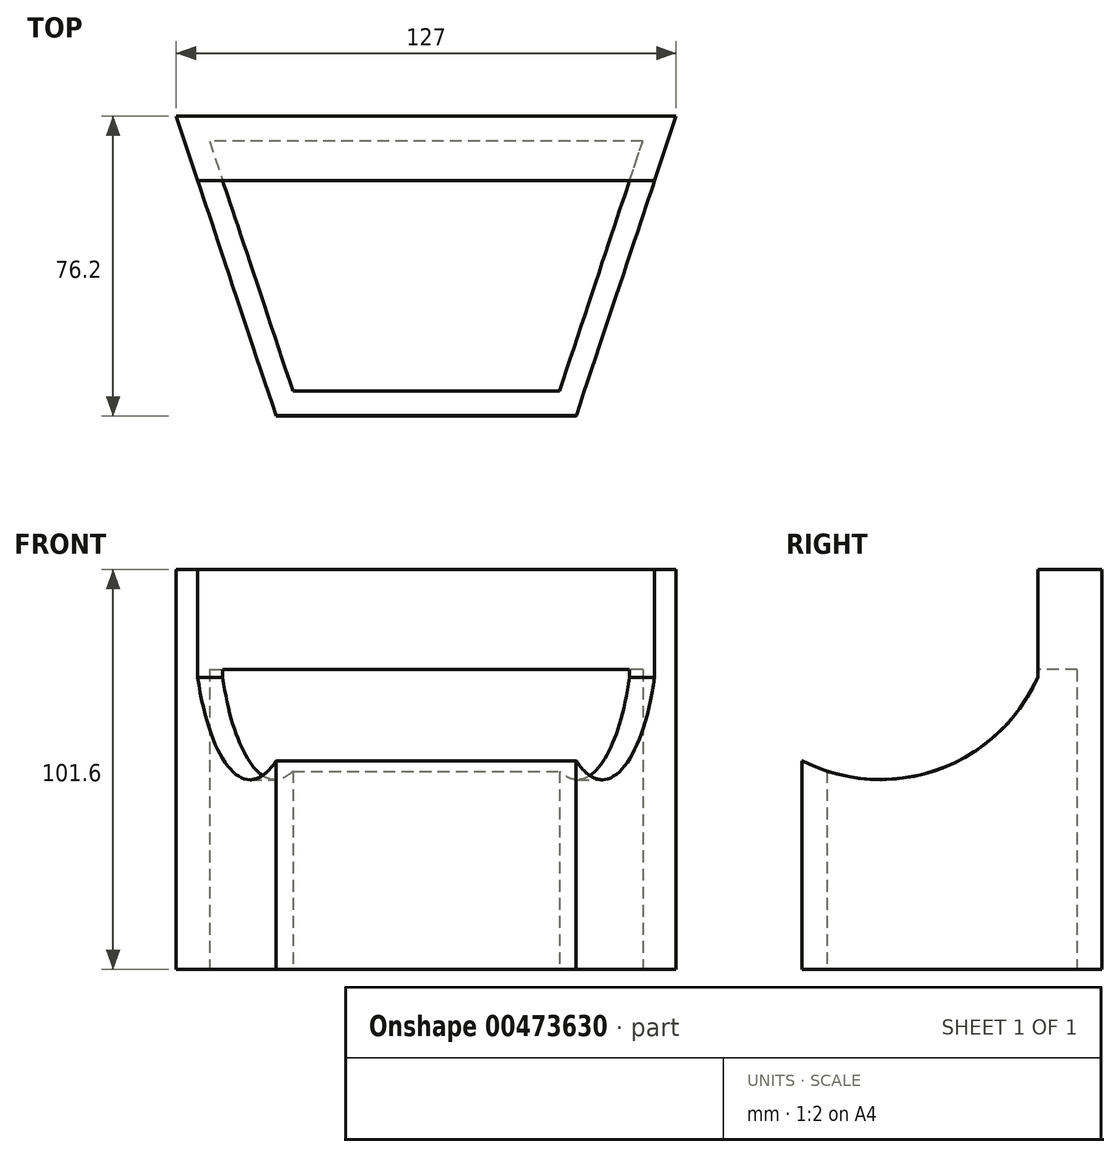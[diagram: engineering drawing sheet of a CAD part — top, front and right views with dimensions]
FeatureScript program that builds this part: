
annotation { "Feature Type Name" : "Feature", "Feature Type Description" : "" }
export const myFeature = defineFeature(function(context is Context, id is Id, definition is map)
    precondition{}
    {
        {
            var Q0;
            Q0=qCreatedBy(makeId("Top.planeOp"),FACE);
            var sketch = newSketch(context, id + "F0", { "sketchPlane" : qUnion([Q0])});
            skLineSegment(sketch, "E0.bottom", {"start": v(-38.1, -62.14) * mm, "end": v(38.1, -62.14) * mm});
            skLineSegment(sketch, "E1", {"start": v(-63.5, 14.06) * mm, "end": v(63.5, 14.06) * mm});
            skLineSegment(sketch, "E2", {"start": v(63.5, 14.06) * mm, "end": v(38.1, -62.14) * mm});
            skLineSegment(sketch, "E3", {"start": v(-38.1, -62.14) * mm, "end": v(-63.5, 14.06) * mm});
            skPoint(sketch, "E4", {"position": v(0, 14.06) * mm});
            skSolve(sketch);
        }
        {
            var Q0;
            Q0=makeQuery(id+"F0.imprint","IMPRINT",FACE,{"disambiguationData":[TD([[makeQuery(id+"F0.imprint","IMPRINT",EDGE,{"derivedFrom":sQuery(id+"F0.wireOp",EDGE,"E0.bottom")}),1.0]])]});
            extrude(context, id + "F1", {"entities" : qUnion([Q0]), "depth" : 101.6 * mm});
        }
        {
            var Q0;
            Q0=qCreatedBy(makeId("Right.planeOp"),FACE);
            cPlane(context, id + "F2", {"entities" : qUnion([Q0]), "cplaneType" : CPlaneType.OFFSET, "offset" : 63.5 * mm, "width" : 152.4 * mm, "height" : 152.4 * mm});
        }
        {
            var Q0;
            Q0=qCreatedBy(id+"F2.planeOp",FACE);
            var sketch = newSketch(context, id + "F3", { "sketchPlane" : qUnion([Q0])});
            skArc(sketch, "E5", {"start": v(-33.98, 110.4) * mm, "mid": v(-46.42, 109.44) * mm, "end": v(-57.74, 104.2) * mm});
            skLineSegment(sketch, "E6", {"start": v(-2.29, 74.18) * mm, "end": v(-2.29, 110.4) * mm});
            skLineSegment(sketch, "E7", {"start": v(-2.29, 110.4) * mm, "end": v(-33.98, 110.4) * mm});
            skPoint(sketch, "E8.top.end.orphan", {"position": v(13.85, 0) * mm});
            skLineSegment(sketch, "E9.bottom", {"start": v(-68.36, 104.2) * mm, "end": v(-57.74, 104.2) * mm});
            skLineSegment(sketch, "E9.left", {"start": v(-68.36, 104.2) * mm, "end": v(-68.36, 91.7) * mm});
            skLineSegment(sketch, "E10", {"start": v(-68.36, 91.7) * mm, "end": v(-68.36, 52.96) * mm});
            skLineSegment(sketch, "E11", {"start": v(-68.36, 52.96) * mm, "end": v(-62.04, 52.96) * mm});
            skArc(sketch, "E12", {"start": v(-62.04, 52.96) * mm, "mid": v(-27.6, 50.7) * mm, "end": v(-2.29, 74.18) * mm});
            skSolve(sketch);
        }
        {
            var Q0;
            Q0=makeQuery(id+"F3.imprint","IMPRINT",FACE,{"disambiguationData":[TD([[makeQuery(id+"F3.imprint","IMPRINT",EDGE,{"derivedFrom":sQuery(id+"F3.wireOp",EDGE,"E5")}),1.0]])]});
            extrude(context, id + "F4", {"entities" : qUnion([Q0]), "operationType" : NewBodyOperationType.REMOVE, "oppositeDirection" : true, "depth" : 127 * mm});
        }
        {
            var Q0;
            Q0=qCreatedBy(makeId("Top.planeOp"),FACE);
            var sketch = newSketch(context, id + "F5", { "sketchPlane" : qUnion([Q0])});
            skLineSegment(sketch, "E13", {"start": v(-55.03, 7.7) * mm, "end": v(-33.87, -55.8) * mm});
            skLineSegment(sketch, "E14", {"start": v(-33.87, -55.8) * mm, "end": v(33.87, -55.8) * mm});
            skLineSegment(sketch, "E15", {"start": v(33.87, -55.8) * mm, "end": v(55.03, 7.7) * mm});
            skLineSegment(sketch, "E16", {"start": v(55.03, 7.7) * mm, "end": v(-55.03, 7.7) * mm});
            skPoint(sketch, "E17.end.orphan", {"position": v(-61.38, 7.7) * mm});
            skPoint(sketch, "E18.0.1.end.orphan", {"position": v(38.1, -62.14) * mm});
            skPoint(sketch, "E18.0.1.start.orphan", {"position": v(63.5, 14.06) * mm});
            skPoint(sketch, "E19.orphan", {"position": v(-38.1, -62.14) * mm});
            skPoint(sketch, "E18.0.3.end.orphan", {"position": v(-63.5, 14.06) * mm});
            skSolve(sketch);
        }
        {
            var Q0;
            Q0 = qSketchRegion(id + "F5", true);
            extrude(context, id + "F6", {"entities" : qUnion([Q0]), "operationType" : NewBodyOperationType.REMOVE, "depth" : 76.2 * mm});
        }
    });
